# Revit family: Ruth
name_source: partatom
category: Furniture
units: mm (PartAtom-declared; Revit-internal decimal feet)

## family parameters
Always vertical = Yes
Cut with Voids When Loaded = No
OmniClass Number = 23.40.20.00
OmniClass Title = General Furniture and Specialties
Room Calculation Point = No
Shared = No
Work Plane-Based = No

## types (6) — shared parameters
CSI MasterFormat 2014 Code = 12 00 00
CSI MasterFormat 2014 Title = Furnishings
Depth = 440 mm
Description = Stapel- och upphängningsbar stol Ruth i massiv vitbetsad björk
Edition number = 1
Height = 734 mm
IFC Classification = Furniture
Keynote = Ruth, Stol, chair, sono, form, o miljö
Length = 495 mm
Manufacturer = Form o miljö
ManufacturerName = Form o miljö
ManufacturerURL = https://formomiljo.se
Model = Ruth
OmniClass Code = 23-40 20 00
OmniClass Description = General Furniture
Product group = Ruth
Product name = Ruth stol
URL = https://www.sonobrands.se
Uniclass 2015 Code = EF_40_30
Uniclass 2015 Name = Furnishings
Weight = 4,2 kg
zero-valued in all types: Default Elevation

## per-type parameters (varying)
| type | Primary Material | Product SKU |
| Birch | Birch | 432162 |
| Black | Birch black | 432185 |
| White | Birch white | 432190 |
| Birch with absorbent | Birch | 432163 |
| Black with absorbent | Birch black | 432186 |
| White with absorbent | Birch white | 432191 |

## geometry (parser evidence)
native form markers: Sweep x3
no freeform markers — native parametric forms only
